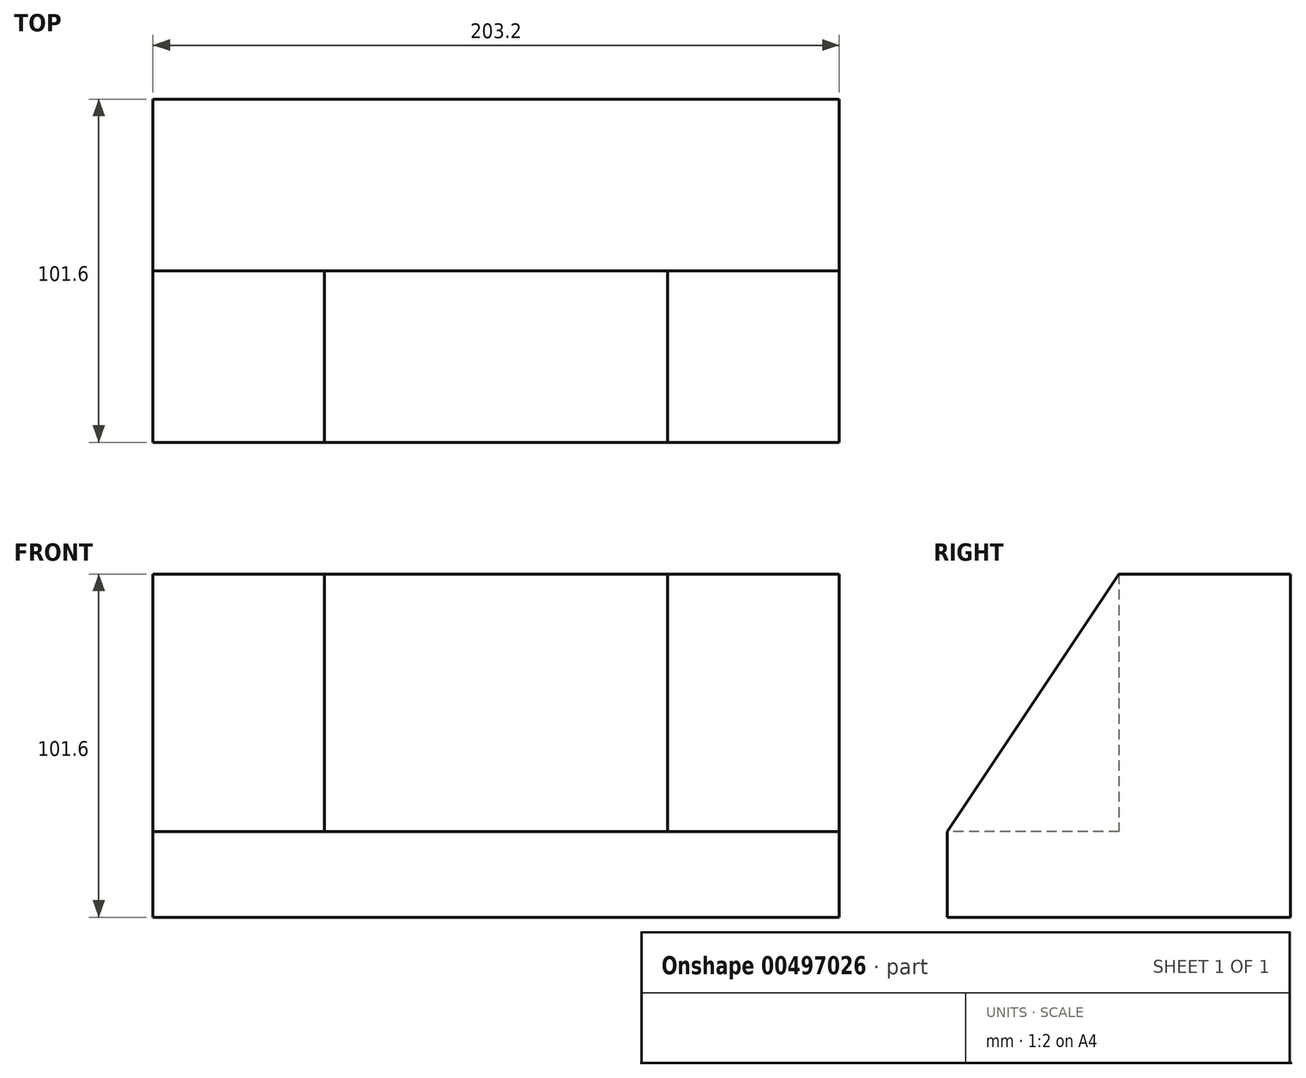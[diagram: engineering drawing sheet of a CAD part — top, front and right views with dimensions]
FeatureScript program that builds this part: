
annotation { "Feature Type Name" : "Feature", "Feature Type Description" : "" }
export const myFeature = defineFeature(function(context is Context, id is Id, definition is map)
    precondition{}
    {
        {
            var Q0;
            Q0=qCreatedBy(makeId("Front.planeOp"),FACE);
            var sketch = newSketch(context, id + "F0", { "sketchPlane" : qUnion([Q0])});
            skLineSegment(sketch, "E0.bottom", {"start": v(0, 0) * mm, "end": v(203.2, 0) * mm});
            skLineSegment(sketch, "E0.top", {"start": v(0, 101.6) * mm, "end": v(203.2, 101.6) * mm});
            skLineSegment(sketch, "E0.left", {"start": v(0, 0) * mm, "end": v(0, 101.6) * mm});
            skLineSegment(sketch, "E0.right", {"start": v(203.2, 0) * mm, "end": v(203.2, 101.6) * mm});
            skLineSegment(sketch, "E1", {"start": v(50.8, 101.6) * mm, "end": v(50.8, 25.4) * mm});
            skLineSegment(sketch, "E2", {"start": v(50.8, 25.4) * mm, "end": v(0, 25.4) * mm});
            skLineSegment(sketch, "E3", {"start": v(152.4, 101.6) * mm, "end": v(152.4, 25.4) * mm});
            skLineSegment(sketch, "E4", {"start": v(152.4, 25.4) * mm, "end": v(203.2, 25.4) * mm});
            skLineSegment(sketch, "E5", {"start": v(50.8, 25.4) * mm, "end": v(152.4, 25.4) * mm});
            skSolve(sketch);
        }
        {
            var Q0;
            Q0 = qSketchRegion(id + "F0", true);
            extrude(context, id + "F1", {"entities" : qUnion([Q0]), "depth" : 101.6 * mm});
        }
        {
            var Q0;
            Q0=makeQuery(id+"F1.opExtrude","CAP_FACE",FACE,{"disambiguationData":[OSD([sQuery(id+"F0.wireOp",EDGE,"E0.bottom"),sQuery(id+"F0.wireOp",EDGE,"E0.top"),sQuery(id+"F0.wireOp",EDGE,"E0.left"),sQuery(id+"F0.wireOp",EDGE,"E0.right")])],"isStart":false});
            var sketch = newSketch(context, id + "F2", { "sketchPlane" : qUnion([Q0])});
            skLineSegment(sketch, "E6", {"start": v(50.8, 101.6) * mm, "end": v(50.8, 25.4) * mm});
            skLineSegment(sketch, "E7", {"start": v(50.8, 25.4) * mm, "end": v(0, 25.4) * mm});
            skLineSegment(sketch, "E8", {"start": v(152.4, 101.6) * mm, "end": v(152.4, 25.4) * mm});
            skLineSegment(sketch, "E9", {"start": v(152.4, 25.4) * mm, "end": v(203.2, 25.4) * mm});
            skLineSegment(sketch, "E10", {"start": v(50.8, 25.4) * mm, "end": v(152.4, 25.4) * mm});
            skSolve(sketch);
        }
        {
            var Q0;
            {var subQ0=sQuery(id+"F2.wireOp",EDGE,"E6");Q0=makeQuery(id+"F2.imprint","IMPRINT",FACE,{"disambiguationData":[TD([[makeQuery(id+"F2.imprint","IMPRINT",EDGE,{"derivedFrom":subQ0}),1.0]])]});}
            extrude(context, id + "F3", {"entities" : qUnion([Q0]), "operationType" : NewBodyOperationType.REMOVE, "oppositeDirection" : true, "depth" : 50.8 * mm});
        }
        {
            var Q0;
            Q0=makeQuery(id+"F3.boolean.opBoolean","COPY",FACE,{"derivedFrom":makeQuery(id+"F3.opExtrude","SWEPT_FACE",FACE,{"disambiguationData":[OSD([sQuery(id+"F2.wireOp",EDGE,"E6")])]})});
            var sketch = newSketch(context, id + "F4", { "sketchPlane" : qUnion([Q0])});
            skLineSegment(sketch, "E11", {"start": v(-50.8, 101.6) * mm, "end": v(-101.6, 25.4) * mm});
            skSolve(sketch);
        }
        {
            var Q0;
            Q0=makeQuery(id+"F3.boolean.opBoolean","COPY",FACE,{"derivedFrom":makeQuery(id+"F3.opExtrude","SWEPT_FACE",FACE,{"disambiguationData":[OSD([sQuery(id+"F2.wireOp",EDGE,"E8")])]})});
            var sketch = newSketch(context, id + "F5", { "sketchPlane" : qUnion([Q0])});
            skLineSegment(sketch, "E12", {"start": v(50.8, 101.6) * mm, "end": v(101.6, 25.4) * mm});
            skSolve(sketch);
        }
        {
            var Q0;
            Q0=makeQuery(id+"F4.imprint","IMPRINT",FACE,{"disambiguationData":[TD([[makeQuery(id+"F4.imprint","IMPRINT",EDGE,{"derivedFrom":sQuery(id+"F4.wireOp",EDGE,"E11")}),-1.0]])]});
            extrude(context, id + "F6", {"entities" : qUnion([Q0]), "operationType" : NewBodyOperationType.REMOVE, "oppositeDirection" : true, "depth" : 50.8 * mm});
        }
        {
            var Q0;
            Q0=makeQuery(id+"F5.imprint","IMPRINT",FACE,{"disambiguationData":[TD([[makeQuery(id+"F5.imprint","IMPRINT",EDGE,{"derivedFrom":sQuery(id+"F5.wireOp",EDGE,"E12")}),1.0]])]});
            extrude(context, id + "F7", {"entities" : qUnion([Q0]), "operationType" : NewBodyOperationType.REMOVE, "oppositeDirection" : true, "depth" : 50.8 * mm});
        }
    });
